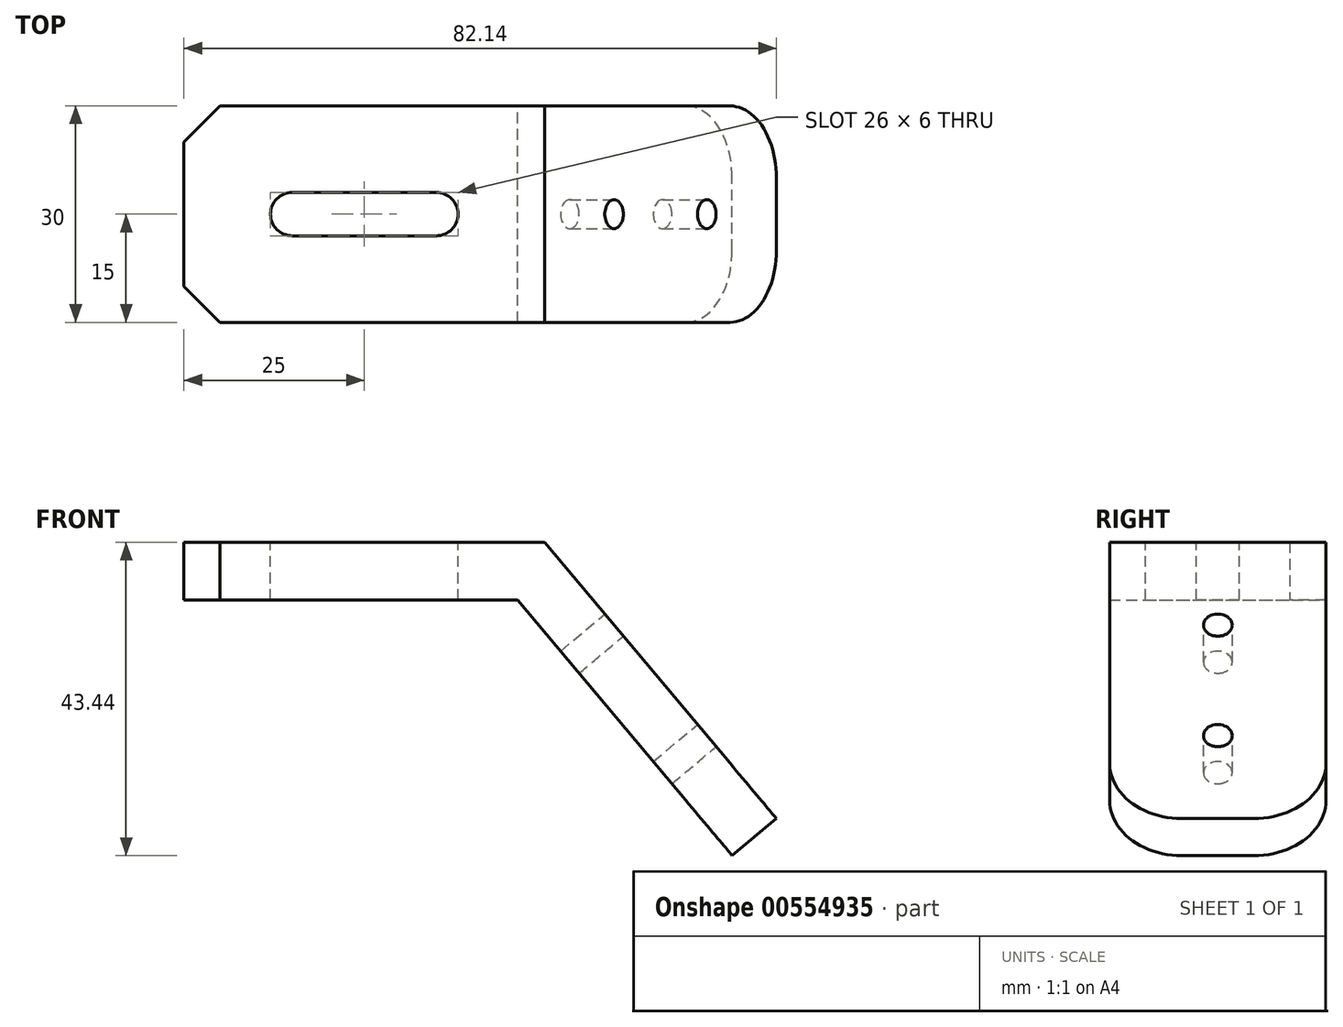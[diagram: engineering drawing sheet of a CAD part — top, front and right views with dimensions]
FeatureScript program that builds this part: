
annotation { "Feature Type Name" : "Feature", "Feature Type Description" : "" }
export const myFeature = defineFeature(function(context is Context, id is Id, definition is map)
    precondition{}
    {
        {
            var Q0;
            Q0=qCreatedBy(makeId("Front.planeOp"),FACE);
            var sketch = newSketch(context, id + "F0", { "sketchPlane" : qUnion([Q0])});
            skLineSegment(sketch, "E0", {"start": v(0, 0) * mm, "end": v(46.27, 0) * mm});
            skLineSegment(sketch, "E1", {"start": v(46.27, 0) * mm, "end": v(76.01, -35.44) * mm});
            skLineSegment(sketch, "E2.0", {"start": v(50, 8) * mm, "end": v(82.14, -30.3) * mm});
            skLineSegment(sketch, "E2.1", {"start": v(0, 8) * mm, "end": v(50, 8) * mm});
            skLineSegment(sketch, "E3", {"start": v(0, 8) * mm, "end": v(0, 0) * mm});
            skLineSegment(sketch, "E4", {"start": v(76.01, -35.44) * mm, "end": v(82.14, -30.3) * mm});
            skSolve(sketch);
        }
        {
            var Q0;
            Q0 = qSketchRegion(id + "F0", true);
            extrude(context, id + "F1", {"entities" : qUnion([Q0]), "endBound" : BoundingType.SYMMETRIC, "depth" : 30 * mm, "offsetDistance" : 25 * mm});
        }
        {
            var Q0;
            Q0=makeQuery(id+"F1.opExtrude","SWEPT_FACE",FACE,{"disambiguationData":[OSD([sQuery(id+"F0.wireOp",EDGE,"E2.1")])]});
            var sketch = newSketch(context, id + "F2", { "sketchPlane" : qUnion([Q0])});
            skLineSegment(sketch, "E5", {"start": v(15, 0) * mm, "end": v(35, 0) * mm});
            skArc(sketch, "E6.0.startCap", {"start": v(15, -3) * mm, "mid": v(12, 0) * mm, "end": v(15, 3) * mm});
            skArc(sketch, "E6.0.endCap", {"start": v(35, 3) * mm, "mid": v(38, 0) * mm, "end": v(35, -3) * mm});
            skLineSegment(sketch, "E6.0.left", {"start": v(15, 3) * mm, "end": v(35, 3) * mm});
            skLineSegment(sketch, "E6.0.right", {"start": v(15, -3) * mm, "end": v(35, -3) * mm});
            skSolve(sketch);
        }
        {
            var Q0;
            Q0 = qSketchRegion(id + "F2", true);
            extrude(context, id + "F3", {"entities" : qUnion([Q0]), "operationType" : NewBodyOperationType.REMOVE, "endBound" : BoundingType.THROUGH_ALL, "oppositeDirection" : true, "depth" : 25 * mm, "offsetDistance" : 25 * mm});
        }
        {
            var Q0;
            Q0=makeQuery(id+"F1.opExtrude","SWEPT_FACE",FACE,{"disambiguationData":[OSD([sQuery(id+"F0.wireOp",EDGE,"E2.0")])]});
            var sketch = newSketch(context, id + "F4", { "sketchPlane" : qUnion([Q0])});
            skPoint(sketch, "E7", {"position": v(0, -61.01) * mm});
            skPoint(sketch, "E8", {"position": v(0, -41.01) * mm});
            skSolve(sketch);
        }
        {
            var Q0;
            Q0=sQuery(id+"F4.wireOp",VERTEX,"E8");
            var Q1;
            Q1=sQuery(id+"F4.wireOp",VERTEX,"E7");
            var Q2;
            Q2=makeQuery(id+"F1.opExtrude","SWEPT_BODY",BODY,{"disambiguationData":[OSD([sQuery(id+"F0.wireOp",EDGE,"E0"),sQuery(id+"F0.wireOp",EDGE,"E1"),sQuery(id+"F0.wireOp",EDGE,"E2.0"),sQuery(id+"F0.wireOp",EDGE,"E2.1"),sQuery(id+"F0.wireOp",EDGE,"E3"),sQuery(id+"F0.wireOp",EDGE,"E4")])]});
            hole(context, id + "F5", {"style" : HoleStyle.SIMPLE, "endStyle" : HoleEndStyle.THROUGH, "holeDiameter" : 4 * mm, "isTappedThrough" : true, "tappedDepth" : 12 * mm, "tapClearance" : 3, "locations" : qUnion([Q0, Q1]), "scope" : qUnion([Q2])});
        }
        {
            var Q0;
            Q0=makeQuery(id+"F1.opExtrude","CAP_EDGE",EDGE,{"disambiguationData":[OSD([sQuery(id+"F0.wireOp",EDGE,"E4")])],"isStart":false});
            var Q1;
            Q1=makeQuery(id+"F1.opExtrude","CAP_EDGE",EDGE,{"disambiguationData":[OSD([sQuery(id+"F0.wireOp",EDGE,"E4")])],"isStart":true});
            fillet(context, id + "F6", {"entities" : qUnion([Q0, Q1]), "radius" : 10 * mm, "tangentPropagation" : true, "allowEdgeOverflow" : false});
        }
        {
            var Q0;
            Q0=makeQuery(id+"F1.opExtrude","CAP_EDGE",EDGE,{"disambiguationData":[OSD([sQuery(id+"F0.wireOp",EDGE,"E3")])],"isStart":false});
            var Q1;
            Q1=makeQuery(id+"F1.opExtrude","CAP_EDGE",EDGE,{"disambiguationData":[OSD([sQuery(id+"F0.wireOp",EDGE,"E3")])],"isStart":true});
            chamfer(context, id + "F7", {"entities" : qUnion([Q0, Q1]), "width" : 5 * mm, "tangentPropagation" : true});
        }
    });
